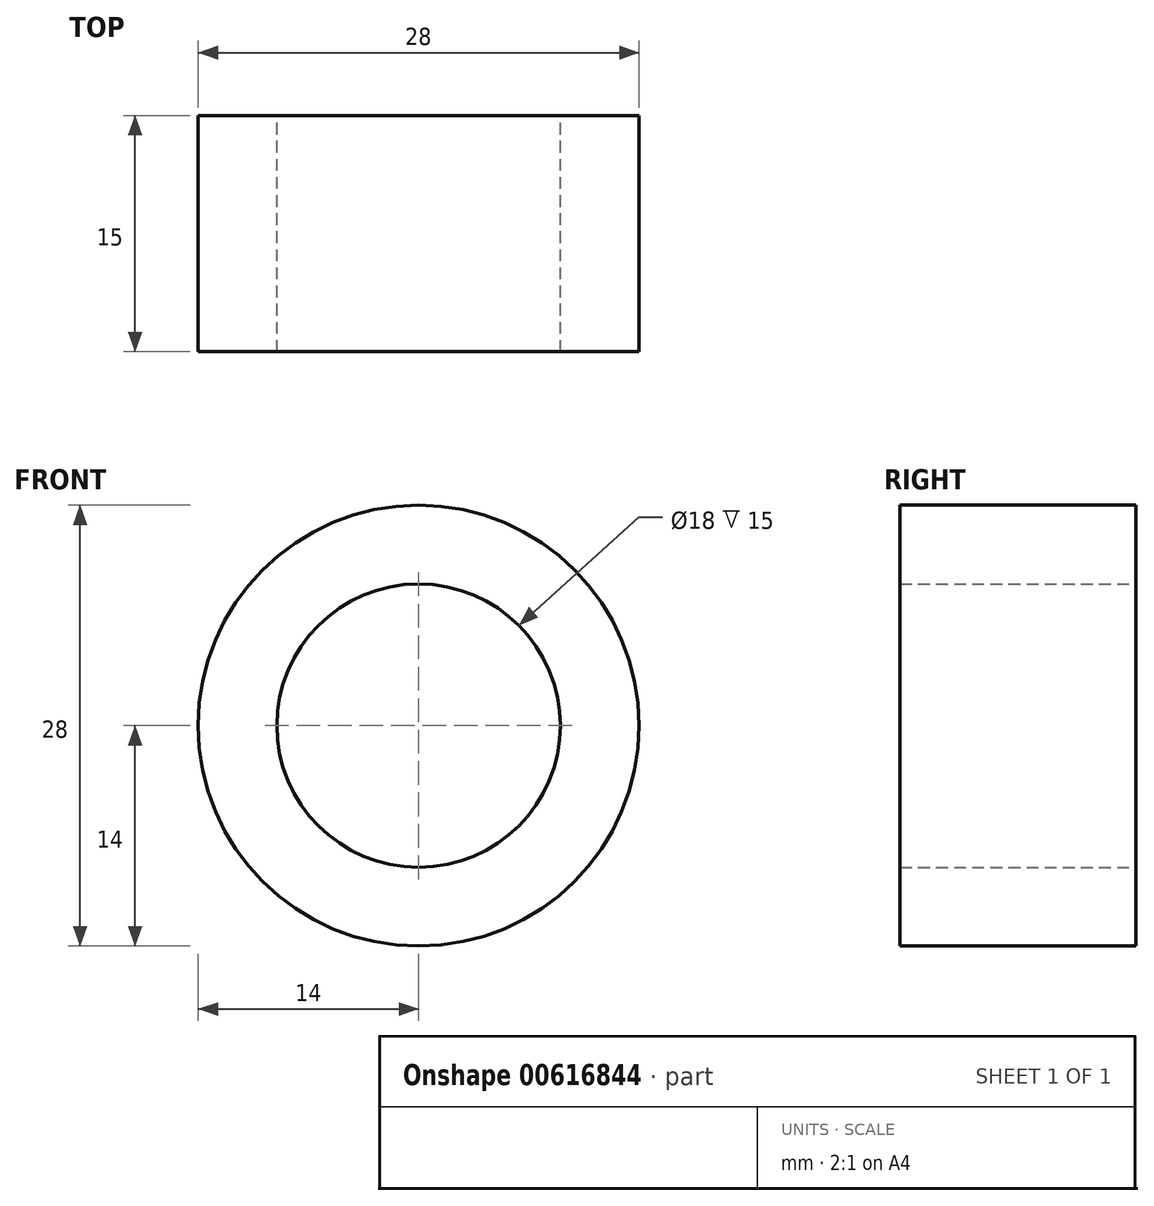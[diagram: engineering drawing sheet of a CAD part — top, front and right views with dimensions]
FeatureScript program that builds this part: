
annotation { "Feature Type Name" : "Feature", "Feature Type Description" : "" }
export const myFeature = defineFeature(function(context is Context, id is Id, definition is map)
    precondition{}
    {
        {
            var Q0;
            Q0=qCreatedBy(makeId("Front.planeOp"),FACE);
            var sketch = newSketch(context, id + "F0", { "sketchPlane" : qUnion([Q0])});
            skCircle(sketch, "E0", {"center": v(0, 0) * mm, "radius": 9 * mm});
            skCircle(sketch, "E1", {"center": v(0, 0) * mm, "radius": 14 * mm});
            skSolve(sketch);
        }
        {
            var Q0;
            Q0 = qSketchRegion(id + "F0", true);
            extrude(context, id + "F1", {"entities" : qUnion([Q0]), "depth" : 15 * mm, "offsetDistance" : 25 * mm});
        }
    });
